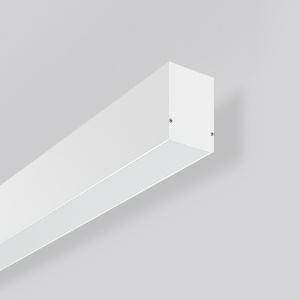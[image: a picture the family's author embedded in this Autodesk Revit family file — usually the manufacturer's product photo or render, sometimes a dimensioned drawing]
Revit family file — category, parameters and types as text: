
# Revit family: less_is_more_50_312612_002_0b17
name_source: partatom
category: Lighting Fixtures
units: mm (PartAtom-declared; Revit-internal decimal feet)

## family parameters
Cut with Voids When Loaded = No
Host = Face
Light Source = No
Part Type = Normal
Room Calculation Point = No
Round Connector Dimension = Use Diameter
Shared = No

## types (1)
- LESS IS MORE 50 (1 x LED Modul 830, 3900 lm, 3000)
    Apparent Load = 30 VA
    CIE Flux Codes = 48 80 96 50 100
    Color Rendering = 80
    Color Temperature = 3000
    Default Elevation = 1800 mm
    Description = Series: LESS IS MORE 50
Linear wall luminaires. Housing: extruded aluminium profile, powder-coated. End cap aluminium powder-coated. Diffuser made of non-yellowing plastic (PMMA), opal. Direct 50%, indirect 50% light emission. Suitable for Wall (surface). LED unit with integrated converter interchangeable and removable. Suitable for through-wiring. With sensors or as a safety luminaire on request. 
Colour: traffic white, matt (RAL 9016)
Length: 1687 mm
Width: 67 mm
Height: 75 mm
Lamp: LED
Socket: without socket
Colour temperature: 3000K
Colour rendering index (CRI): 80
Light source: LED
Socket lamp2: Without base
Colour temperature: 3000K
Colour rendering index (CRI) 2: 80
System power: 30 W
Rated luminous flux: 3900 lm
Luminous efficiency: 130 lm/W
Control gear: Regulated power supply
Control gear: Regulated power supply
Protection class: I
Type of protection: IP 20
    Height = 75 mm
    Lamp = 1 x LED Modul 830
    Lamp Light Flux = 3900 lm
    Lamp count = 1
    Length = 1687 mm
    Lifetime = 50000 h
    Luminous efficacy = 130 lm/W
    Manufacturer = RZB
    ModVariant = No
    Model = 312612.002
    Mounting Place = Wall
    Mounting Type = Surface mounted
    Number of Poles = 1
    OnlyDefault = Yes
    Power Factor = 1
    Product Name = LESS IS MORE 50
    Product group = Surface mounted LED linear luminaires
    ProductGroupID = 2007
    Protection Class = Protection class I
    Protection Degree = IP 20
    RLX_Detail_Level = 1
    RLX_Emergency_Light_Flux = 0 lm
    RLX_Emergency_Type = 0
    RLX_Emergency_Type_DB = No
    RlxData = <blob elided: 39645 chars, md5=4b49220c>
    Socket = socket
    Standby Power = 0 W
    System Light Flux = 3900 lm
    System Power = 30 W
    Type Comments = Product without accessories
    Type Image = 312606.002.jpg
    URL = http://relux.com
    VarID = ---
    Voltage = 0 V
    Weight = 0.00 kg
    Width = 67 mm

## geometry (parser evidence)
native form markers: Blend x4, Sweep x9
no freeform markers — native parametric forms only
